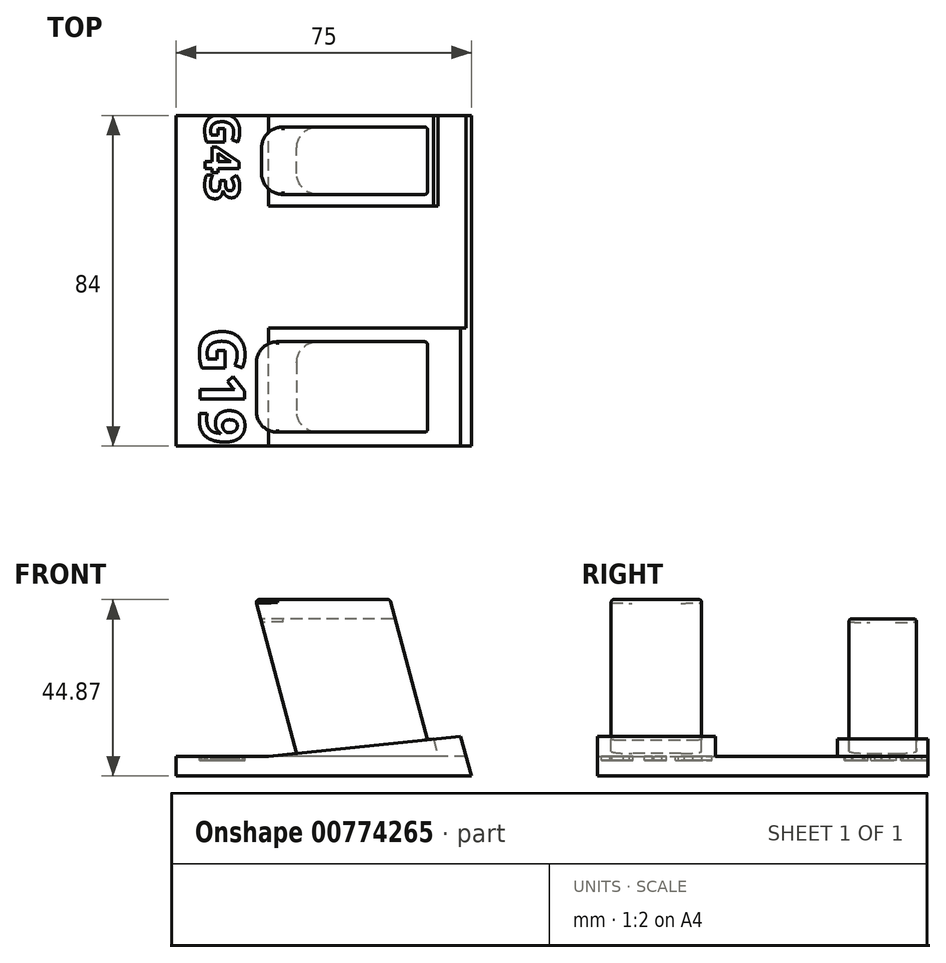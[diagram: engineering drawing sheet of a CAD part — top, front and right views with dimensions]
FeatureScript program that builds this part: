
annotation { "Feature Type Name" : "Feature", "Feature Type Description" : "" }
export const myFeature = defineFeature(function(context is Context, id is Id, definition is map)
    precondition{}
    {
        {
            var Q0;
            Q0=qCreatedBy(makeId("Front.planeOp"),FACE);
            var sketch = newSketch(context, id + "F0", { "sketchPlane" : qUnion([Q0])});
            skLineSegment(sketch, "E0", {"start": v(-17.08, 0) * mm, "end": v(17.08, 0) * mm, "construction": true});
            skLineSegment(sketch, "E1", {"start": v(17.08, 0) * mm, "end": v(5.06, 44.87) * mm, "construction": true});
            skLineSegment(sketch, "E2", {"start": v(-29.1, 44.87) * mm, "end": v(-17.08, 0) * mm, "construction": true});
            skLineSegment(sketch, "E3", {"start": v(5.7, 44.87) * mm, "end": v(17.73, 0) * mm, "construction": true});
            skLineSegment(sketch, "E4", {"start": v(-17.73, 0) * mm, "end": v(-29.75, 44.87) * mm, "construction": true});
            skLineSegment(sketch, "E5", {"start": v(-29.75, 44.87) * mm, "end": v(5.7, 44.87) * mm, "construction": true});
            skLineSegment(sketch, "E6", {"start": v(0, 0) * mm, "end": v(-12.02, 44.87) * mm, "construction": true});
            skLineSegment(sketch, "E7", {"start": v(-75, 0) * mm, "end": v(75, 0) * mm, "construction": true});
            skLineSegment(sketch, "E8", {"start": v(-24.46, 0) * mm, "end": v(-25.8, 5) * mm, "construction": true});
            skLineSegment(sketch, "E9", {"start": v(-24.46, 0) * mm, "end": v(25.75, 0) * mm, "construction": true});
            skLineSegment(sketch, "E10", {"start": v(25.75, 0) * mm, "end": v(23.04, 10.13) * mm, "construction": true});
            skLineSegment(sketch, "E11", {"start": v(23.04, 10.13) * mm, "end": v(-25.8, 5) * mm, "construction": true});
            skLineSegment(sketch, "E12", {"start": v(-25.8, 5) * mm, "end": v(24.41, 5) * mm, "construction": true});
            skLineSegment(sketch, "E13", {"start": v(-17.08, 0) * mm, "end": v(-29.1, 44.87) * mm});
            skLineSegment(sketch, "E14", {"start": v(-29.1, 44.87) * mm, "end": v(4.12, 48.37) * mm, "construction": true});
            skLineSegment(sketch, "E15", {"start": v(17.08, 0) * mm, "end": v(-17.08, 0) * mm});
            skLineSegment(sketch, "E16", {"start": v(-29.1, 44.87) * mm, "end": v(5.06, 44.87) * mm});
            skLineSegment(sketch, "E17", {"start": v(5.06, 44.87) * mm, "end": v(17.08, 0) * mm});
            skSolve(sketch);
        }
        {
            var Q0;
            Q0=qSketchRegion(id+"F0",true);
            extrude(context, id + "F1", {"entities" : qUnion([Q0]), "endBound" : BoundingType.SYMMETRIC, "depth" : 23 * mm, "offsetDistance" : 25 * mm});
        }
        {
            var Q0;
            Q0=qCreatedBy(makeId("Front.planeOp"),FACE);
            var sketch = newSketch(context, id + "F2", { "sketchPlane" : qUnion([Q0])});
            skLineSegment(sketch, "E18", {"start": v(-25.8, 5) * mm, "end": v(-24.46, 0) * mm, "construction": true});
            skLineSegment(sketch, "E19", {"start": v(23.04, 10.13) * mm, "end": v(-25.8, 5) * mm});
            skLineSegment(sketch, "E20", {"start": v(-25.8, 5) * mm, "end": v(-25.8, 0) * mm});
            skLineSegment(sketch, "E21", {"start": v(-25.8, 0) * mm, "end": v(23.04, 0) * mm, "construction": true});
            skLineSegment(sketch, "E22", {"start": v(23.04, 0) * mm, "end": v(23.04, 10.13) * mm, "construction": true});
            skLineSegment(sketch, "E23", {"start": v(-25.8, 0) * mm, "end": v(25.75, 0) * mm});
            skLineSegment(sketch, "E24", {"start": v(25.75, 0) * mm, "end": v(23.04, 10.13) * mm});
            skSolve(sketch);
        }
        {
            var Q0;
            Q0=qSketchRegion(id+"F2",true);
            extrude(context, id + "F3", {"entities" : qUnion([Q0]), "operationType" : NewBodyOperationType.ADD, "endBound" : BoundingType.SYMMETRIC, "depth" : 30 * mm, "offsetDistance" : 25 * mm});
        }
        {
            var Q0;
            Q0=makeQuery(id+"F1.opExtrude","CAP_EDGE",EDGE,{"disambiguationData":[OSD([sQuery(id+"F0.wireOp",EDGE,"E13")])],"isStart":true});
            var Q1;
            Q1=makeQuery(id+"F1.opExtrude","CAP_EDGE",EDGE,{"disambiguationData":[OSD([sQuery(id+"F0.wireOp",EDGE,"E13")])],"isStart":false});
            fillet(context, id + "F4", {"entities" : qUnion([Q0, Q1]), "radius" : 5.25 * mm, "tangentPropagation" : true, "allowEdgeOverflow" : false});
        }
        {
            var Q0;
            Q0=makeQuery(id+"F3.opExtrude","CAP_FACE",FACE,{"disambiguationData":[OSD([sQuery(id+"F2.wireOp",EDGE,"E19"),sQuery(id+"F2.wireOp",EDGE,"E20"),sQuery(id+"F2.wireOp",EDGE,"E23"),sQuery(id+"F2.wireOp",EDGE,"E24")])],"isStart":false});
            var sketch = newSketch(context, id + "F5", { "sketchPlane" : qUnion([Q0])});
            skLineSegment(sketch, "E25.bottom", {"start": v(25.75, 0) * mm, "end": v(-49.25, 0) * mm});
            skLineSegment(sketch, "E25.top", {"start": v(24.41, 5) * mm, "end": v(-49.25, 5) * mm});
            skLineSegment(sketch, "E25.left", {"start": v(25.75, 0) * mm, "end": v(24.41, 5) * mm});
            skLineSegment(sketch, "E25.right", {"start": v(-49.25, 0) * mm, "end": v(-49.25, 5) * mm});
            skSolve(sketch);
        }
        {
            var Q0;
            Q0 = qSketchRegion(id + "F5", true);
            extrude(context, id + "F6", {"entities" : qUnion([Q0]), "operationType" : NewBodyOperationType.ADD, "oppositeDirection" : true, "depth" : 84 * mm, "offsetDistance" : 25 * mm});
        }
        {
            var Q0;
            Q0=makeQuery(id+"F6.opExtrude","CAP_FACE",FACE,{"disambiguationData":[OSD([sQuery(id+"F5.wireOp",EDGE,"E25.bottom"),sQuery(id+"F5.wireOp",EDGE,"E25.top"),sQuery(id+"F5.wireOp",EDGE,"E25.left"),sQuery(id+"F5.wireOp",EDGE,"E25.right")])],"isStart":false});
            var sketch = newSketch(context, id + "F7", { "sketchPlane" : qUnion([Q0])});
            skLineSegment(sketch, "E26", {"start": v(-25.75, 0) * mm, "end": v(-23.04, 10.13) * mm});
            skLineSegment(sketch, "E27", {"start": v(-23.04, 10.13) * mm, "end": v(25.8, 5) * mm});
            skLineSegment(sketch, "E28", {"start": v(25.8, 5) * mm, "end": v(25.8, 0) * mm});
            skLineSegment(sketch, "E29", {"start": v(25.8, 0) * mm, "end": v(-25.75, 0) * mm});
            skSolve(sketch);
        }
        {
            var Q0;
            Q0 = qSketchRegion(id + "F7", true);
            extrude(context, id + "F8", {"entities" : qUnion([Q0]), "operationType" : NewBodyOperationType.ADD, "oppositeDirection" : true, "depth" : 23 * mm, "offsetDistance" : 25 * mm});
        }
        {
            var Q0;
            Q0=makeQuery(id+"F8.boolean.opBoolean","MERGE",FACE,{"derivedFrom":[makeQuery(id+"F6.opExtrude","CAP_FACE",FACE,{"disambiguationData":[OSD([sQuery(id+"F5.wireOp",EDGE,"E25.bottom"),sQuery(id+"F5.wireOp",EDGE,"E25.top"),sQuery(id+"F5.wireOp",EDGE,"E25.left"),sQuery(id+"F5.wireOp",EDGE,"E25.right")])],"isStart":false}),makeQuery(id+"F8.opExtrude","CAP_FACE",FACE,{"disambiguationData":[OSD([sQuery(id+"F7.wireOp",EDGE,"E26"),sQuery(id+"F7.wireOp",EDGE,"E27"),sQuery(id+"F7.wireOp",EDGE,"E28"),sQuery(id+"F7.wireOp",EDGE,"E29")])],"isStart":true})]});
            cPlane(context, id + "F9", {"entities" : qUnion([Q0]), "cplaneType" : CPlaneType.OFFSET, "offset" : 23 / 2 * mm, "oppositeDirection" : true, "width" : 150 * mm, "height" : 150 * mm});
        }
        {
            var Q0;
            Q0=qCreatedBy(id+"F9.planeOp",FACE);
            var sketch = newSketch(context, id + "F10", { "sketchPlane" : qUnion([Q0])});
            skLineSegment(sketch, "E30", {"start": v(-17.08, 0) * mm, "end": v(-6.37, 39.98) * mm});
            skLineSegment(sketch, "E31", {"start": v(-6.37, 39.98) * mm, "end": v(27.8, 39.98) * mm});
            skLineSegment(sketch, "E32", {"start": v(27.8, 39.98) * mm, "end": v(17.08, 0) * mm});
            skLineSegment(sketch, "E33", {"start": v(17.08, 0) * mm, "end": v(-17.08, 0) * mm});
            skLineSegment(sketch, "E34", {"start": v(-6.37, 39.98) * mm, "end": v(-5.43, 43.48) * mm, "construction": true});
            skLineSegment(sketch, "E35", {"start": v(-5.43, 43.48) * mm, "end": v(27.8, 39.98) * mm, "construction": true});
            skSolve(sketch);
        }
        {
            var Q0;
            Q0 = qSketchRegion(id + "F10", true);
            extrude(context, id + "F11", {"entities" : qUnion([Q0]), "operationType" : NewBodyOperationType.ADD, "endBound" : BoundingType.SYMMETRIC, "depth" : 17.15 * mm, "offsetDistance" : 25 * mm});
        }
        {
            var Q0;
            Q0=makeQuery(id+"F11.opExtrude","CAP_EDGE",EDGE,{"disambiguationData":[OSD([sQuery(id+"F10.wireOp",EDGE,"E32")])],"isStart":false});
            var Q1;
            Q1=makeQuery(id+"F11.opExtrude","CAP_EDGE",EDGE,{"disambiguationData":[OSD([sQuery(id+"F10.wireOp",EDGE,"E32")])],"isStart":true});
            fillet(context, id + "F12", {"entities" : qUnion([Q0, Q1]), "radius" : 5.33 * mm, "tangentPropagation" : true, "allowEdgeOverflow" : false});
        }
        {
            var Q0;
            Q0=makeQuery(id+"F8.boolean.opBoolean","MERGE",FACE,{"derivedFrom":[makeQuery(id+"F6.opExtrude","CAP_FACE",FACE,{"disambiguationData":[OSD([sQuery(id+"F5.wireOp",EDGE,"E25.bottom"),sQuery(id+"F5.wireOp",EDGE,"E25.top"),sQuery(id+"F5.wireOp",EDGE,"E25.left"),sQuery(id+"F5.wireOp",EDGE,"E25.right")])],"isStart":false}),makeQuery(id+"F8.opExtrude","CAP_FACE",FACE,{"disambiguationData":[OSD([sQuery(id+"F7.wireOp",EDGE,"E26"),sQuery(id+"F7.wireOp",EDGE,"E27"),sQuery(id+"F7.wireOp",EDGE,"E28"),sQuery(id+"F7.wireOp",EDGE,"E29")])],"isStart":true})]});
            var sketch = newSketch(context, id + "F13", { "sketchPlane" : qUnion([Q0])});
            skLineSegment(sketch, "E36", {"start": v(-16.1, 9.4) * mm, "end": v(-23.04, 10.13) * mm});
            skLineSegment(sketch, "E37", {"start": v(-16.1, 9.4) * mm, "end": v(-17.28, 5) * mm});
            skLineSegment(sketch, "E38", {"start": v(-23.04, 10.13) * mm, "end": v(-24.41, 5) * mm});
            skLineSegment(sketch, "E39", {"start": v(-24.41, 5) * mm, "end": v(-17.28, 5) * mm});
            skLineSegment(sketch, "E40", {"start": v(-16.1, 9.4) * mm, "end": v(-16.1, 0) * mm, "construction": true});
            skLineSegment(sketch, "E41", {"start": v(-14.6, 9.25) * mm, "end": v(-14.6, 0) * mm, "construction": true});
            skSolve(sketch);
        }
        {
            var Q0;
            Q0 = qSketchRegion(id + "F13", true);
            var Q1;
            Q1=makeQuery(id+"F8.opExtrude","CAP_FACE",FACE,{"disambiguationData":[OSD([sQuery(id+"F7.wireOp",EDGE,"E26"),sQuery(id+"F7.wireOp",EDGE,"E27"),sQuery(id+"F7.wireOp",EDGE,"E28"),sQuery(id+"F7.wireOp",EDGE,"E29")])],"isStart":false});
            extrude(context, id + "F14", {"entities" : qUnion([Q0, Q1]), "operationType" : NewBodyOperationType.REMOVE, "endBound" : BoundingType.UP_TO_NEXT, "oppositeDirection" : true, "depth" : 25 * mm, "offsetDistance" : 25 * mm});
        }
        {
            var Q0;
            Q0=makeQuery(id+"F1.opExtrude","CAP_EDGE",EDGE,{"disambiguationData":[OSD([sQuery(id+"F0.wireOp",EDGE,"E17")])],"isStart":false});
            var Q1;
            Q1=makeQuery(id+"F1.opExtrude","CAP_EDGE",EDGE,{"disambiguationData":[OSD([sQuery(id+"F0.wireOp",EDGE,"E17")])],"isStart":true});
            var Q2;
            Q2=makeQuery(id+"F11.opExtrude","CAP_EDGE",EDGE,{"disambiguationData":[OSD([sQuery(id+"F10.wireOp",EDGE,"E30")])],"isStart":true});
            var Q3;
            Q3=makeQuery(id+"F11.opExtrude","CAP_EDGE",EDGE,{"disambiguationData":[OSD([sQuery(id+"F10.wireOp",EDGE,"E30")])],"isStart":false});
            var Q4;
            Q4=makeQuery(id+"F11.opExtrude","SWEPT_FACE",FACE,{"disambiguationData":[OSD([sQuery(id+"F10.wireOp",EDGE,"E31")])]});
            var Q5;
            Q5=makeQuery(id+"F1.opExtrude","SWEPT_FACE",FACE,{"disambiguationData":[OSD([sQuery(id+"F0.wireOp",EDGE,"E16")])]});
            fillet(context, id + "F15", {"entities" : qUnion([Q0, Q1, Q2, Q3, Q4, Q5]), "radius" : .75 * mm, "tangentPropagation" : true, "allowEdgeOverflow" : false});
        }
        {
            var Q0;
            {var subQ0=sQuery(id+"F5.wireOp",EDGE,"E25.top");Q0=makeQuery(id+"F14.boolean.opBoolean","MERGE",FACE,{"derivedFrom":[makeQuery(id+"F6.opExtrude","SWEPT_FACE",FACE,{"disambiguationData":[OSD([subQ0])]}),makeQuery(id+"F14.opExtrude","SWEPT_FACE",FACE,{"disambiguationData":[OSD([subQ0,sQuery(id+"F7.wireOp",EDGE,"E26"),sQuery(id+"F7.wireOp",EDGE,"E27"),sQuery(id+"F7.wireOp",EDGE,"E28"),sQuery(id+"F7.wireOp",EDGE,"E29")])]}),makeQuery(id+"F14.opExtrude","SWEPT_FACE",FACE,{"disambiguationData":[OSD([sQuery(id+"F13.wireOp",EDGE,"E39")])]})]});}
            var sketch = newSketch(context, id + "F16", { "sketchPlane" : qUnion([Q0])});
            skLineSegment(sketch, "E42", {"start": v(-25.8, 57.5) * mm, "end": v(-49.25, 57.5) * mm, "construction": true});
            skLineSegment(sketch, "E43", {"start": v(-25.8, 0) * mm, "end": v(-49.25, 0) * mm, "construction": true});
            skText(sketch, "E44", { "text": "G43", "fontName": "OpenSans-Bold.ttf"});
            skLineSegment(sketch, "E45", {"start": v(-37.52, 69) * mm, "end": v(-37.52, 46) * mm, "construction": true});
            skText(sketch, "E46", { "text": "G19", "fontName": "OpenSans-Bold.ttf"});
            skLineSegment(sketch, "E47", {"start": v(-37.52, 69) * mm, "end": v(-37.52, -15) * mm, "construction": true});
            skLineSegment(sketch, "E48", {"start": v(-37.52, -15) * mm, "end": v(-37.52, 15) * mm, "construction": true});
            const initialGuessF16  = {"E44": [-0.0419, 0.07, 0, -1, 0.00875], "E46": [-0.04322, 0.015, 0, -1, 0.0114]};
            skSetInitialGuess(sketch, initialGuessF16);
            skSolve(sketch);
        }
        {
            var Q0;
            Q0 = qSketchRegion(id + "F16", true);
            extrude(context, id + "F17", {"entities" : qUnion([Q0]), "operationType" : NewBodyOperationType.REMOVE, "oppositeDirection" : true, "depth" : 1 * mm, "offsetDistance" : 25 * mm});
        }
    });
